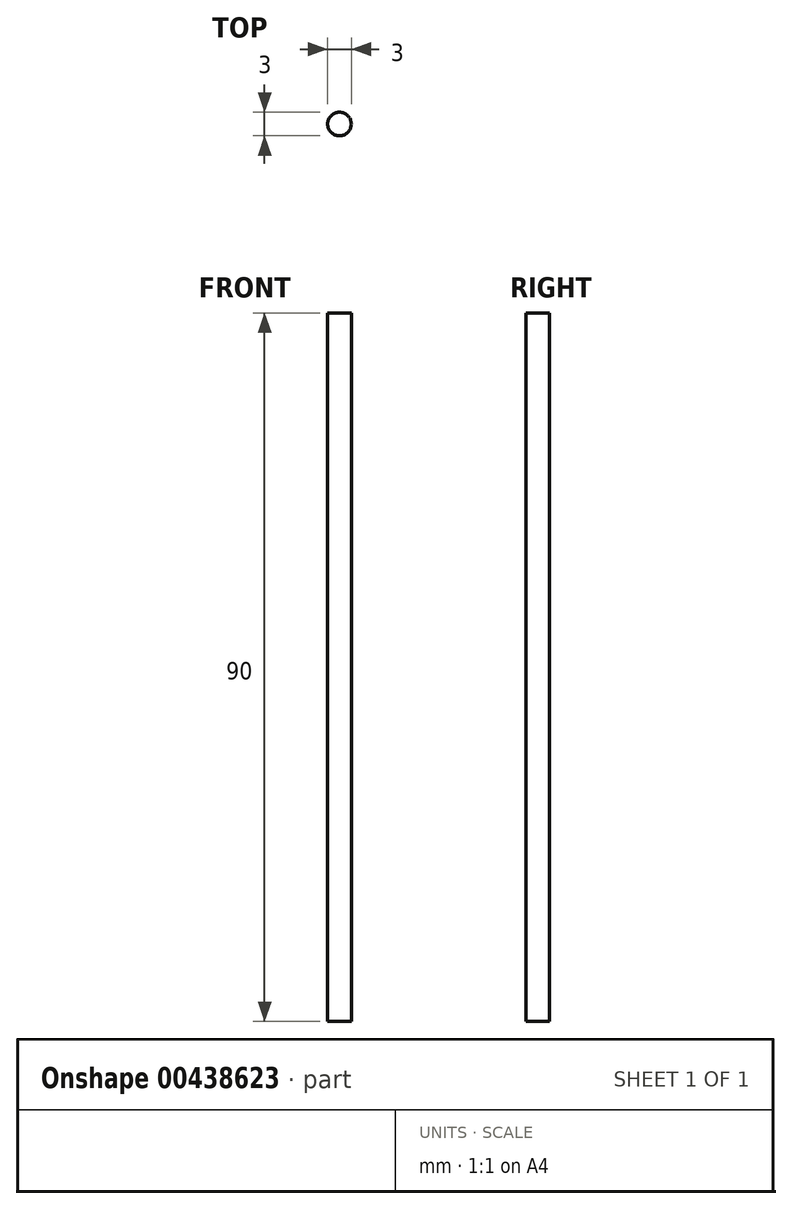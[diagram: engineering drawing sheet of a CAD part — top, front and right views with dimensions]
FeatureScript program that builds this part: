
annotation { "Feature Type Name" : "Feature", "Feature Type Description" : "" }
export const myFeature = defineFeature(function(context is Context, id is Id, definition is map)
    precondition{}
    {
        {
            var Q0;
            Q0=qCreatedBy(makeId("Top.planeOp"),FACE);
            var sketch = newSketch(context, id + "F0", { "sketchPlane" : qUnion([Q0])});
            skCircle(sketch, "E0", {"center": v(0, 0) * mm, "radius": 1.5 * mm});
            skSolve(sketch);
        }
        {
            var Q0;
            Q0 = qSketchRegion(id + "F0", true);
            extrude(context, id + "F1", {"entities" : qUnion([Q0]), "depth" : 90 * mm});
        }
    });
